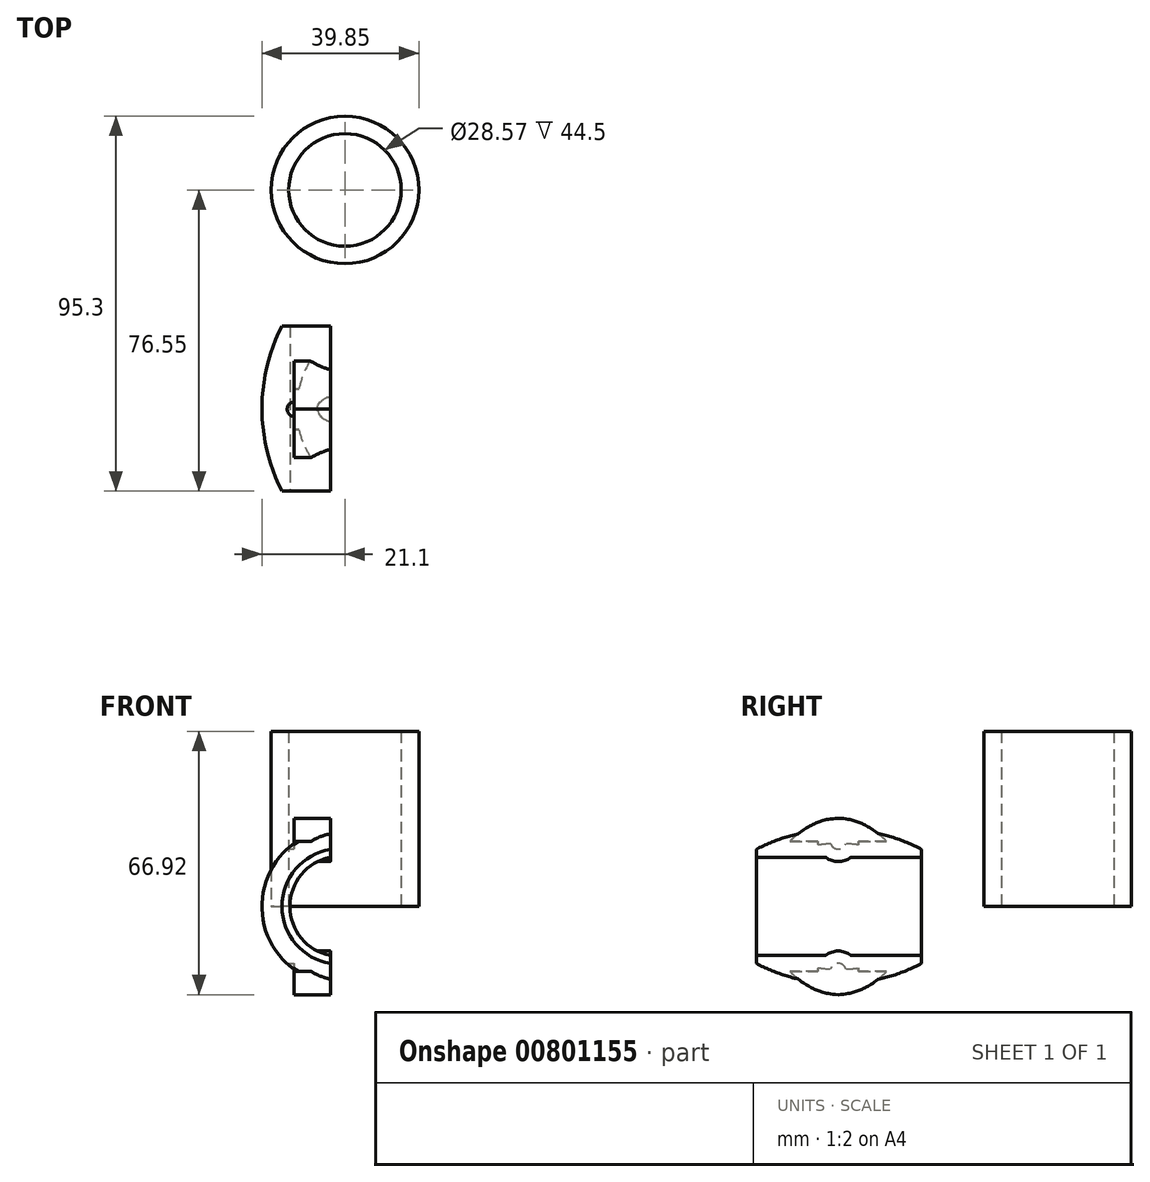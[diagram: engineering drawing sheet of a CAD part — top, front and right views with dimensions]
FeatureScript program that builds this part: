
annotation { "Feature Type Name" : "Feature", "Feature Type Description" : "" }
export const myFeature = defineFeature(function(context is Context, id is Id, definition is map)
    precondition{}
    {
        {
            var Q0;
            Q0=qCreatedBy(makeId("Top.planeOp"),FACE);
            var sketch = newSketch(context, id + "F0", { "sketchPlane" : qUnion([Q0])});
            skCircle(sketch, "E0", {"center": v(0, 0) * mm, "radius": 14.29 * mm});
            skCircle(sketch, "E1", {"center": v(0, 0) * mm, "radius": 18.75 * mm});
            skSolve(sketch);
        }
        {
            var Q0;
            Q0 = qSketchRegion(id + "F0", true);
            extrude(context, id + "F1", {"entities" : qUnion([Q0]), "depth" : 44.5 * mm, "offsetDistance" : 25 * mm});
        }
        {
            var Q0;
            Q0=qCreatedBy(makeId("Right.planeOp"),FACE);
            cPlane(context, id + "F2", {"entities" : qUnion([Q0]), "cplaneType" : CPlaneType.OFFSET, "offset" : 20 * mm, "width" : 150 * mm, "height" : 150 * mm});
        }
        {
            var Q0;
            Q0=qCreatedBy(makeId("Top.planeOp"),FACE);
            var sketch = newSketch(context, id + "F3", { "sketchPlane" : qUnion([Q0])});
            skLineSegment(sketch, "E2", {"start": v(-68.7, -50.73) * mm, "end": v(-35.5, -50.73) * mm});
            skCircle(sketch, "E3", {"center": v(-68.7, -50.73) * mm, "radius": 3.6 * mm});
            skCircle(sketch, "E4", {"center": v(-35.5, -50.73) * mm, "radius": 3.6 * mm});
            skPoint(sketch, "E5", {"position": v(-65.1, -50.73) * mm});
            skPoint(sketch, "E6", {"position": v(-39.1, -50.73) * mm});
            skLineSegment(sketch, "E7", {"start": v(-52.1, -50.73) * mm, "end": v(-52.1, -29.73) * mm});
            skLineSegment(sketch, "E8", {"start": v(-14, -55.55) * mm, "end": v(11.4, -55.55) * mm});
            skLineSegment(sketch, "E9", {"start": v(-14, -55.55) * mm, "end": v(-14, -34.55) * mm});
            skLineSegment(sketch, "E10.MirrorCS", {"start": v(-14, -55.55) * mm, "end": v(-14, -76.55) * mm});
            skLineSegment(sketch, "E11", {"start": v(-1.3, -55.55) * mm, "end": v(-1.3, -41.26) * mm});
            skPoint(sketch, "E12.end.orphan", {"position": v(-21.1, -55.55) * mm});
            skPoint(sketch, "E13.MirrorCS.start.orphan", {"position": v(-14, -34.55) * mm});
            skLineSegment(sketch, "E14", {"start": v(-14, -34.55) * mm, "end": v(-16, -34.55) * mm});
            skLineSegment(sketch, "E15.MirrorCS", {"start": v(-14, -76.55) * mm, "end": v(-16, -76.55) * mm});
            skArc(sketch, "E16", {"start": v(-16, -34.55) * mm, "mid": v(-21.1, -55.55) * mm, "end": v(-16, -76.55) * mm});
            skSolve(sketch);
        }
        {
            var Q0;
            {var subQ0=sQuery(id+"F3.wireOp",EDGE,"E9");Q0=makeQuery(id+"F3.imprint","IMPRINT",FACE,{"disambiguationData":[TD([[makeQuery(id+"F3.imprint","IMPRINT",EDGE,{"derivedFrom":subQ0}),1.0]])]});}
            var Q1;
            Q1=sQuery(id+"F3.wireOp",EDGE,"E11");
            revolve(context, id + "F4", {"surfaceOperationType" : NewSurfaceOperationType.NEW, "entities" : qUnion([Q0]), "axis" : qUnion([Q1]), "revolveType" : RevolveType.SYMMETRIC, "angle" : 180 * degree});
        }
        {
            var Q0;
            Q0=qCreatedBy(id+"F2.planeOp",FACE);
            var sketch = newSketch(context, id + "F5", { "sketchPlane" : qUnion([Q0])});
            skLineSegment(sketch, "E17", {"start": v(-83.5, 14.83) * mm, "end": v(-83.5, -14.17) * mm});
            skCircle(sketch, "E18", {"center": v(-83.5, 14.83) * mm, "radius": 2.05 * mm});
            skCircle(sketch, "E19", {"center": v(-83.5, -14.17) * mm, "radius": 2.3 * mm});
            skPoint(sketch, "E20", {"position": v(-83.5, 12.78) * mm});
            skPoint(sketch, "E21", {"position": v(-83.5, -11.87) * mm});
            skLineSegment(sketch, "E22", {"start": v(-55.74, 14.57) * mm, "end": v(-55.74, -14.43) * mm});
            skCircle(sketch, "E23", {"center": v(-55.74, 16.57) * mm, "radius": 2 * mm});
            skCircle(sketch, "E24", {"center": v(-55.74, -16.43) * mm, "radius": 2 * mm});
            skPoint(sketch, "E25", {"position": v(-55.74, 14.57) * mm});
            skPoint(sketch, "E26", {"position": v(-55.74, -14.43) * mm});
            skSolve(sketch);
        }
        {
            var Q0;
            Q0=qCreatedBy(id+"F2.planeOp",FACE);
            var sketch = newSketch(context, id + "F6", { "sketchPlane" : qUnion([Q0])});
            skLineSegment(sketch, "E27.bottom", {"start": v(-84.27, 21.66) * mm, "end": v(-26.5, 21.66) * mm});
            skLineSegment(sketch, "E27.top", {"start": v(-84.27, -24.14) * mm, "end": v(-26.5, -24.14) * mm});
            skLineSegment(sketch, "E27.left", {"start": v(-84.27, 21.66) * mm, "end": v(-84.27, -24.14) * mm});
            skLineSegment(sketch, "E27.right", {"start": v(-26.5, 21.66) * mm, "end": v(-26.5, -24.14) * mm});
            skSolve(sketch);
        }
        {
            var Q0;
            Q0 = qSketchRegion(id + "F6", true);
            extrude(context, id + "F7", {"entities" : qUnion([Q0]), "operationType" : NewBodyOperationType.REMOVE, "oppositeDirection" : true, "depth" : 23.7 * mm, "offsetDistance" : 25 * mm});
        }
        {
            var Q0;
            Q0=makeQuery(id+"F5.imprint","IMPRINT",FACE,{"disambiguationData":[TD([[makeQuery(id+"F5.imprint","IMPRINT",EDGE,{"derivedFrom":sQuery(id+"F5.wireOp",EDGE,"E23")}),1.0]])]});
            var Q1;
            Q1=makeQuery(id+"F5.imprint","IMPRINT",FACE,{"disambiguationData":[TD([[makeQuery(id+"F5.imprint","IMPRINT",EDGE,{"derivedFrom":sQuery(id+"F5.wireOp",EDGE,"E24")}),1.0]])]});
            extrude(context, id + "F8", {"entities" : qUnion([Q0, Q1]), "operationType" : NewBodyOperationType.REMOVE, "oppositeDirection" : true, "depth" : 40 * mm, "offsetDistance" : 25 * mm});
        }
        {
            var Q0;
            Q0=qCreatedBy(makeId("Right.planeOp"),FACE);
            cPlane(context, id + "F9", {"entities" : qUnion([Q0]), "cplaneType" : CPlaneType.OFFSET, "offset" : 13 * mm, "oppositeDirection" : true, "width" : 150 * mm, "height" : 150 * mm});
        }
        {
            var Q0;
            Q0=qCreatedBy(id+"F9.planeOp",FACE);
            var sketch = newSketch(context, id + "F10", { "sketchPlane" : qUnion([Q0])});
            skLineSegment(sketch, "E28", {"start": v(-55.72, 11.4) * mm, "end": v(-55.72, -11.34) * mm});
            skArc(sketch, "E29", {"start": v(-60.87, 16.54) * mm, "mid": v(-55.72, 11.4) * mm, "end": v(-50.57, 16.54) * mm});
            skArc(sketch, "E30", {"start": v(-50.57, -16.54) * mm, "mid": v(-55.72, -11.34) * mm, "end": v(-60.87, -16.54) * mm});
            skLineSegment(sketch, "E31", {"start": v(-50.57, 16.54) * mm, "end": v(-43.45, 16.54) * mm});
            skFitSpline(sketch, "E32", {"points": [v(-55.72, 22.42) * mm, v(-50.93, 21.52) * mm, v(-47.84, 20.06) * mm, v(-43.45, 16.54) * mm], "startDerivative": vector(21.93, -1.42) * mm, "endDerivative": vector(11.12, -11.92) * mm});
            skLineSegment(sketch, "E33", {"start": v(-55.72, 0) * mm, "end": v(-68.94, 0) * mm});
            skFitSpline(sketch, "E34.MirrorCS", {"points": [v(-55.72, 22.42) * mm, v(-60.5, 21.52) * mm, v(-63.6, 20.06) * mm, v(-68, 16.54) * mm], "startDerivative": vector(-21.93, -1.42) * mm, "endDerivative": vector(-11.12, -11.92) * mm});
            skLineSegment(sketch, "E35.MirrorCS", {"start": v(-60.87, 16.54) * mm, "end": v(-68, 16.54) * mm});
            skFitSpline(sketch, "E36.MirrorCS", {"points": [v(-55.72, -22.42) * mm, v(-60.5, -21.52) * mm, v(-63.6, -20.06) * mm, v(-68, -16.54) * mm], "startDerivative": vector(-21.93, 1.42) * mm, "endDerivative": vector(-11.12, 11.92) * mm});
            skFitSpline(sketch, "E37.MirrorCS", {"points": [v(-55.72, -22.42) * mm, v(-50.93, -21.52) * mm, v(-47.84, -20.06) * mm, v(-43.45, -16.54) * mm], "startDerivative": vector(21.93, 1.42) * mm, "endDerivative": vector(11.12, 11.92) * mm});
            skLineSegment(sketch, "E38.MirrorCS", {"start": v(-50.57, -16.54) * mm, "end": v(-43.45, -16.54) * mm});
            skLineSegment(sketch, "E39.MirrorCS", {"start": v(-60.87, -16.54) * mm, "end": v(-68, -16.54) * mm});
            skPoint(sketch, "E40.orphan", {"position": v(-55.72, -16.54) * mm});
            skSolve(sketch);
        }
        {
            var Q0;
            Q0 = qSketchRegion(id + "F10", true);
            extrude(context, id + "F11", {"entities" : qUnion([Q0]), "operationType" : NewBodyOperationType.ADD, "depth" : 9.3 * mm, "offsetDistance" : 25 * mm});
        }
    });
